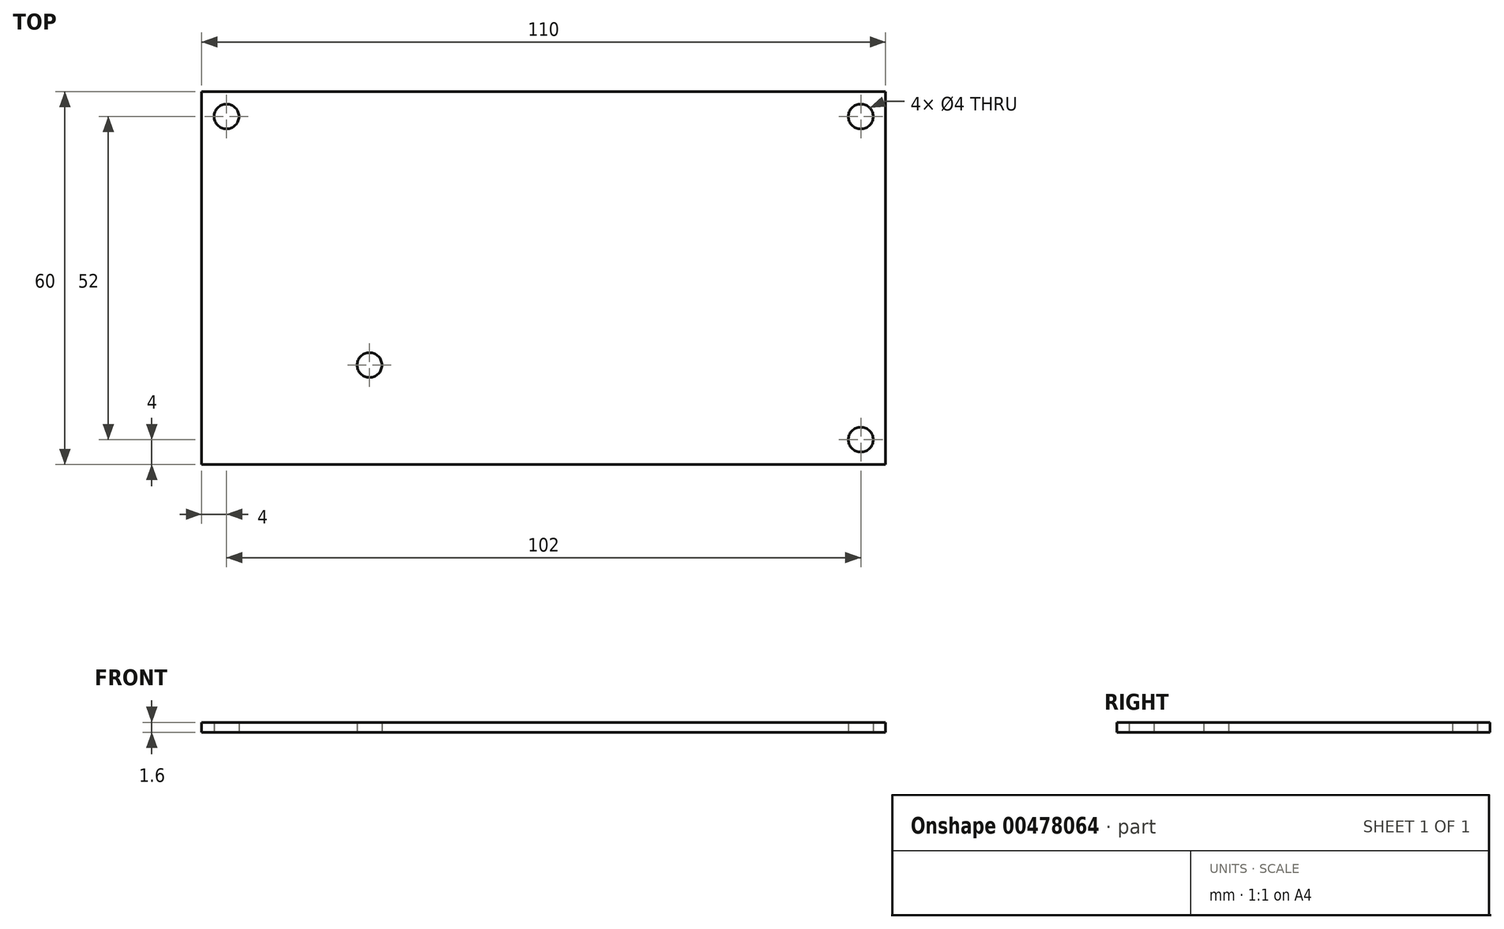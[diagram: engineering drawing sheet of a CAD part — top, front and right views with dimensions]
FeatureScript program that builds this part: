
annotation { "Feature Type Name" : "Feature", "Feature Type Description" : "" }
export const myFeature = defineFeature(function(context is Context, id is Id, definition is map)
    precondition{}
    {
        {
            var Q0;
            Q0=qCreatedBy(makeId("Top.planeOp"),FACE);
            var sketch = newSketch(context, id + "F0", { "sketchPlane" : qUnion([Q0])});
            skLineSegment(sketch, "E0.bottom", {"start": v(55, 30) * mm, "end": v(-55, 30) * mm});
            skLineSegment(sketch, "E0.top", {"start": v(55, -30) * mm, "end": v(-55, -30) * mm});
            skLineSegment(sketch, "E0.left", {"start": v(55, 30) * mm, "end": v(55, -30) * mm});
            skLineSegment(sketch, "E0.right", {"start": v(-55, 30) * mm, "end": v(-55, -30) * mm});
            skPoint(sketch, "E0.middle", {"position": v(0, 0) * mm});
            skCircle(sketch, "E1", {"center": v(-51, 26) * mm, "radius": 2 * mm});
            skCircle(sketch, "E2.1.0.0", {"center": v(51, 26) * mm, "radius": 2 * mm});
            skLineSegment(sketch, "E2.direction1", {"start": v(-51, 26) * mm, "end": v(51, 26) * mm, "construction": true});
            skCircle(sketch, "E3.1.0.0", {"center": v(51, -26) * mm, "radius": 2 * mm});
            skLineSegment(sketch, "E3.direction1", {"start": v(51, 26) * mm, "end": v(51, -26) * mm, "construction": true});
            skCircle(sketch, "E4", {"center": v(-28, -14) * mm, "radius": 2 * mm});
            skSolve(sketch);
        }
        {
            var Q0;
            Q0 = qSketchRegion(id + "F0", true);
            extrude(context, id + "F1", {"entities" : qUnion([Q0]), "depth" : 1.6 * mm});
        }
    });
